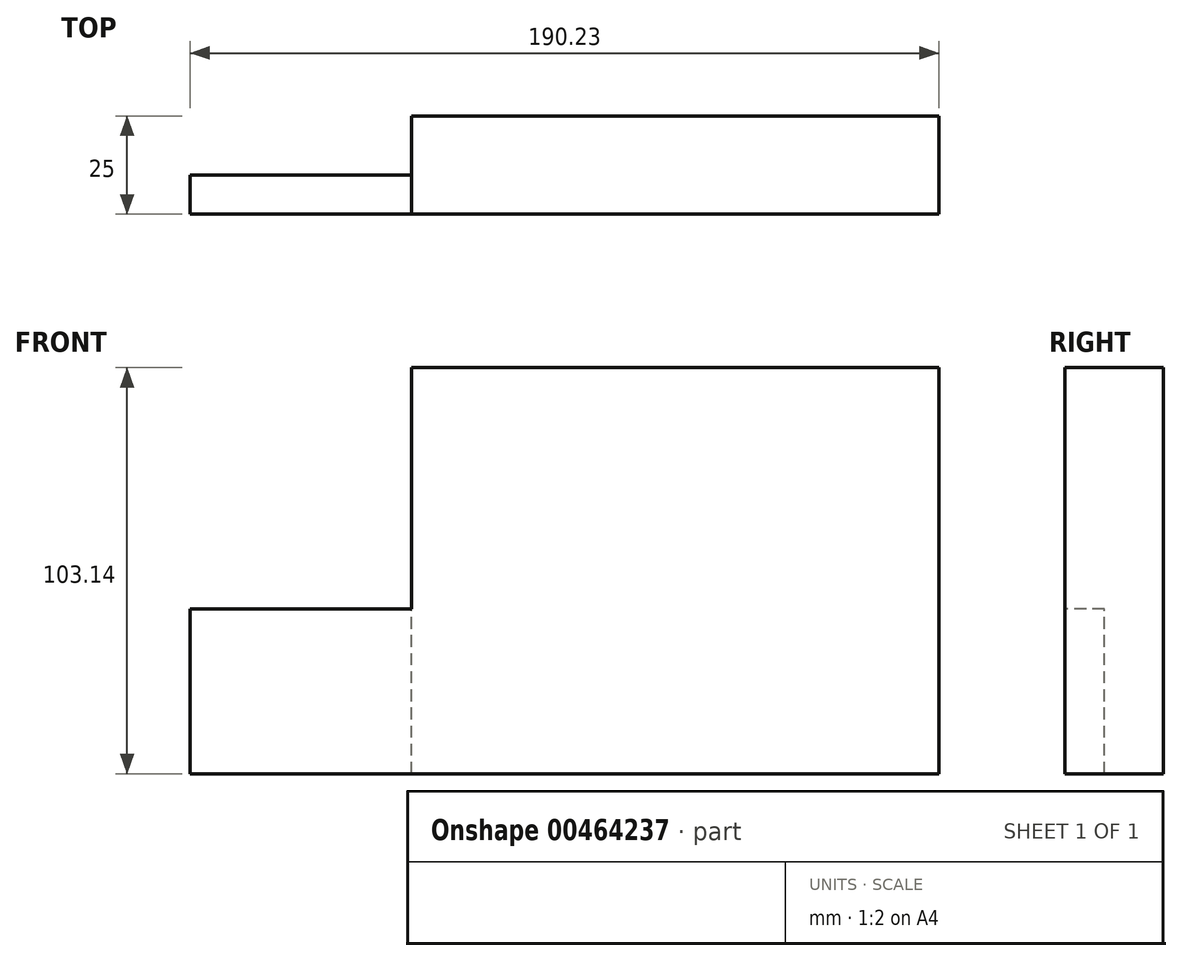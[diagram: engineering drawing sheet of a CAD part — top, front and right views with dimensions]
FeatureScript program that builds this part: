
annotation { "Feature Type Name" : "Feature", "Feature Type Description" : "" }
export const myFeature = defineFeature(function(context is Context, id is Id, definition is map)
    precondition{}
    {
        {
            var Q0;
            Q0=qCreatedBy(makeId("Front.planeOp"),FACE);
            var sketch = newSketch(context, id + "F0", { "sketchPlane" : qUnion([Q0])});
            skLineSegment(sketch, "E0.bottom", {"start": v(0, 0) * mm, "end": v(133.97, 0) * mm});
            skLineSegment(sketch, "E0.top", {"start": v(0, 103.14) * mm, "end": v(133.97, 103.14) * mm});
            skLineSegment(sketch, "E0.left", {"start": v(0, 0) * mm, "end": v(0, 103.14) * mm});
            skLineSegment(sketch, "E0.right", {"start": v(133.97, 0) * mm, "end": v(133.97, 103.14) * mm});
            skSolve(sketch);
        }
        {
            var Q0;
            Q0=makeQuery(id+"F0.imprint","IMPRINT",FACE,{"disambiguationData":[TD([[makeQuery(id+"F0.imprint","IMPRINT",EDGE,{"derivedFrom":sQuery(id+"F0.wireOp",EDGE,"E0.bottom")}),1.0]])]});
            extrude(context, id + "F1", {"entities" : qUnion([Q0]), "oppositeDirection" : true, "depth" : 25 * mm});
        }
        {
            var Q0;
            Q0=qCreatedBy(makeId("Front.planeOp"),FACE);
            var sketch = newSketch(context, id + "F2", { "sketchPlane" : qUnion([Q0])});
            skLineSegment(sketch, "E1.bottom", {"start": v(0, 0) * mm, "end": v(-56.26, 0) * mm});
            skLineSegment(sketch, "E1.top", {"start": v(0, 41.9) * mm, "end": v(-56.26, 41.9) * mm});
            skLineSegment(sketch, "E1.left", {"start": v(0, 0) * mm, "end": v(0, 41.9) * mm});
            skLineSegment(sketch, "E1.right", {"start": v(-56.26, 0) * mm, "end": v(-56.26, 41.9) * mm});
            skSolve(sketch);
        }
        {
            var Q0;
            Q0 = qSketchRegion(id + "F2", true);
            extrude(context, id + "F3", {"entities" : qUnion([Q0]), "operationType" : NewBodyOperationType.ADD, "oppositeDirection" : true, "depth" : 10 * mm});
        }
    });
